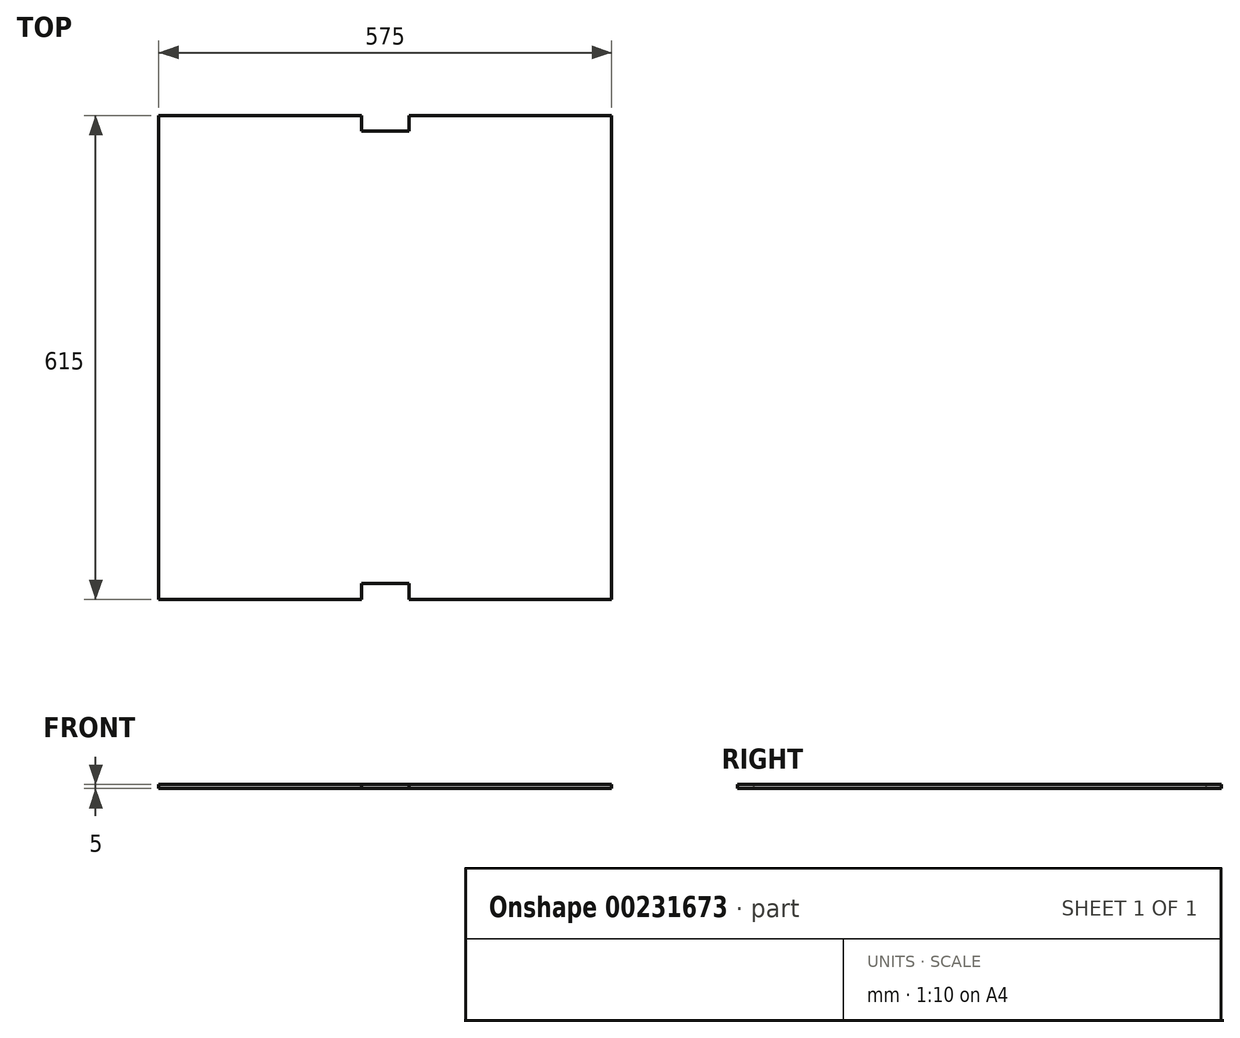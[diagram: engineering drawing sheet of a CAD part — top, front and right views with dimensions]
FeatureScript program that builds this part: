
annotation { "Feature Type Name" : "Feature", "Feature Type Description" : "" }
export const myFeature = defineFeature(function(context is Context, id is Id, definition is map)
    precondition{}
    {
        {
            var Q0;
            Q0=qCreatedBy(makeId("Top.planeOp"),FACE);
            var sketch = newSketch(context, id + "F0", { "sketchPlane" : qUnion([Q0])});
            skLineSegment(sketch, "E0.bottom", {"start": v(287.5, -307.5) * mm, "end": v(30.2, -307.5) * mm});
            skLineSegment(sketch, "E0.top", {"start": v(287.5, 307.5) * mm, "end": v(30.2, 307.5) * mm});
            skLineSegment(sketch, "E0.left", {"start": v(287.5, -307.5) * mm, "end": v(287.5, 307.5) * mm});
            skLineSegment(sketch, "E0.right", {"start": v(-287.5, -307.5) * mm, "end": v(-287.5, 307.5) * mm});
            skPoint(sketch, "E0.middle", {"position": v(0, 0) * mm});
            skLineSegment(sketch, "E1", {"start": v(0, 307.5) * mm, "end": v(0, -307.5) * mm, "construction": true});
            skLineSegment(sketch, "E2", {"start": v(-30.2, 307.5) * mm, "end": v(-30.2, 287.3) * mm});
            skLineSegment(sketch, "E3", {"start": v(-30.2, 287.3) * mm, "end": v(30.2, 287.3) * mm});
            skLineSegment(sketch, "E4", {"start": v(30.2, 287.3) * mm, "end": v(30.2, 307.5) * mm});
            skLineSegment(sketch, "E5.trimOffspring", {"start": v(-30.2, 307.5) * mm, "end": v(-287.5, 307.5) * mm});
            skLineSegment(sketch, "E6", {"start": v(-287.5, 0) * mm, "end": v(287.5, 0) * mm, "construction": true});
            skLineSegment(sketch, "E7.MirrorCS", {"start": v(-30.2, -307.5) * mm, "end": v(-30.2, -287.3) * mm});
            skLineSegment(sketch, "E8.MirrorCS", {"start": v(-30.2, -287.3) * mm, "end": v(30.2, -287.3) * mm});
            skLineSegment(sketch, "E9.MirrorCS", {"start": v(30.2, -287.3) * mm, "end": v(30.2, -307.5) * mm});
            skLineSegment(sketch, "E10.trimOffspring", {"start": v(-30.2, -307.5) * mm, "end": v(-287.5, -307.5) * mm});
            skSolve(sketch);
        }
        {
            var Q0;
            Q0 = qSketchRegion(id + "F0", true);
            extrude(context, id + "F1", {"entities" : qUnion([Q0]), "depth" : 5 * mm});
        }
    });
